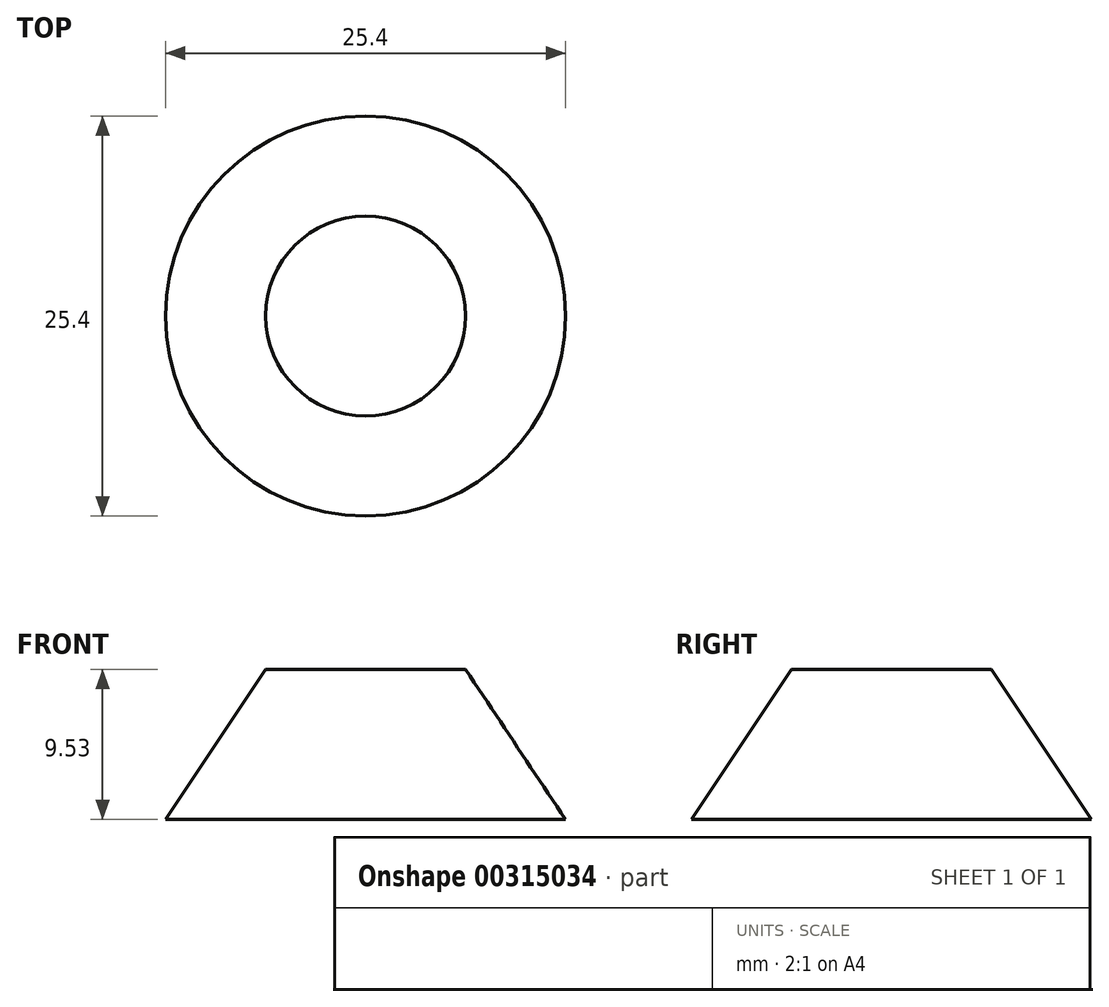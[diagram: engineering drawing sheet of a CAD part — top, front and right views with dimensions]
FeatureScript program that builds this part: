
annotation { "Feature Type Name" : "Feature", "Feature Type Description" : "" }
export const myFeature = defineFeature(function(context is Context, id is Id, definition is map)
    precondition{}
    {
        {
            var Q0;
            Q0=qCreatedBy(makeId("Front.planeOp"),FACE);
            var sketch = newSketch(context, id + "F0", { "sketchPlane" : qUnion([Q0])});
            skLineSegment(sketch, "E0", {"start": v(0, 0) * mm, "end": v(0, -9.53) * mm});
            skLineSegment(sketch, "E1", {"start": v(0, -9.53) * mm, "end": v(-12.7, -9.53) * mm});
            skLineSegment(sketch, "E2", {"start": v(-12.7, -9.53) * mm, "end": v(-6.35, 0) * mm});
            skLineSegment(sketch, "E3", {"start": v(-6.35, 0) * mm, "end": v(0, 0) * mm});
            skSolve(sketch);
        }
        {
            var Q0;
            Q0=makeQuery(id+"F0.imprint","IMPRINT",FACE,{"disambiguationData":[TD([[makeQuery(id+"F0.imprint","IMPRINT",EDGE,{"derivedFrom":sQuery(id+"F0.wireOp",EDGE,"E0")}),-1.0]])]});
            var Q1;
            Q1=sQuery(id+"F0.wireOp",EDGE,"E0");
            revolve(context, id + "F1", {"entities" : qUnion([Q0]), "axis" : qUnion([Q1]), "revolveType" : RevolveType.FULL});
        }
    });
